# Revit family: Mixing_Valve-Emergency-Bradley_Corp-EFX50-S19-2250
name_source: partatom
category: Pipe Accessories
units: mm (PartAtom-declared; Revit-internal decimal feet)

## family parameters
Always vertical = Yes
Cut with Voids When Loaded = No
Part Type = Valve - Breaks Into
Round Connector Dimension = Use Radius
Shared = No
Work Plane-Based = No

## types (1)
- EFX50
    A = 8.75 "
    ADA Compliant = No
    Assembly Code = D2090800
    B = 2.5 "
    Bottom Valve to Bottom Shutoff Inlets = 6.563 "
    Box Depth = 6.375 "
    C = 3.5 "
    Cabinet Depth = 6.5 "
    Cabinet Flange Height = 30 "
    Cabinet Flange Width = 26 "
    Cabinet Height = 28 "
    Cabinet Material = Metal - Bradley Corp - Stainless Steel
    Cabinet Width = 24 "
    Cabinet Window Material = Plastic - Bradley Corp - Plexi-glass
    Center Inlets to Edge = 1.125 "
    D = 5.25 "
    Default Elevation = 0 "
    Description = Emergency Fixture Thermostatic Mixing Valve (EFX60) with Optional Cabinet
    Door Flange Depth = 0.125 "
    E = 12.25 "
    F = 19 "
    Flange Width = 1 "
    G = 3.625 "
    H = 11.375 "
    Height = 12.25 "
    Industry Standards = ANSI Z358.1-2004
    Left Inlet Center to Left of Box = 7.625 "
    Length = 11.375 "
    Manufacturer = Bradley Corporation
    Manufacturer Installation URL - English = https://www.bradleycorp.com
    MasterFormat Number = 22 45 36
    MasterFormat Title = Emergency Fixture Water-Tempering Equipment
    Material = Brass
    Maximum Inlet Temperature = 180˚F (82˚C)
    Maximum Operating Pressure = 125.00 psi
    Minimum Flow = 2 GPM
    Model = S19-2250
    Nut Material = Metal - Bradley Corp - Light Bronze
    OmniClass Code = 23.65.55.14.24
    OmniClass Title = Mixing Valves for Liquid Services
    Outlet Center to Cabinet Back = 2.25 "
    Outlet Center to Piston = 2.5 "
    Percentage of Recycled Content = 0
    Product Page URL = https://www.bradleycorp.com
    Product Tech Data URL - English = https://www.bradleycorp.com
    Set Point = 85˚F (29˚C)
    Set Point Notes = "Refer to Bradley Technical Data for other set points"
    Shutoffs Top to Bottom = 23 "
    Specifications URL = https://www.bradleycorp.com
    Temperature Notes = "Refer to Bradley Technical Data for other temperature ranges"
    Temperature Range = Std. 65˚ (18˚C) to 95˚F (35˚C)
    URL = http://www.bradleycorp.com
    Valve Material = Metal - Bradley Corp - Bronze
    Version = 2.0
    Width = 3.625 "
    Xnpt = 1"
    Xnpt Radius = 1"
    Ynpt = 1"
    Ynpt Radius = 1"
    Znpt = 1"
    Znpt Radius = 0"

## geometry (parser evidence)
native form markers: Blend x30, Sweep x6
no freeform markers — native parametric forms only
